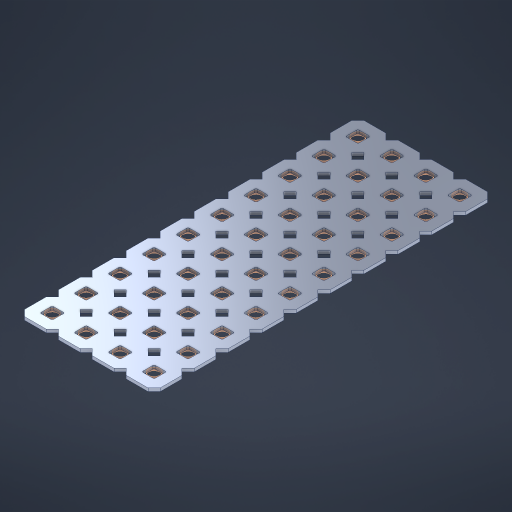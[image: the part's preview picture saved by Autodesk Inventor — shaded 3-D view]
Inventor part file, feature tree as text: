
AUTODESK INVENTOR PART (.ipt)
format: ipt  version: 2023 (Build 270158000, 158)  size: 723,456 bytes
history: native  units: in
note: dims shown in document units (in); Inventor stores cm internally (conversion verified against a paired STEP export)
features: other x41, extrude x39, sketch x2, pattern_linear x1
ambient origin geometry x8: Origin, YZ Plane, XZ Plane, XY Plane, X Axis, Y Axis, Z Axis, Center Point
bodies: Solid1 (feature_tree), Body (feature_tree)
feature tree (83):
  pattern_linear  "Rectangular Pattern1"  Spacing1=0.09in  [1 undecoded]
  sketch  "Sketch1"  dims[d1=0.5in]
  sketch  "Sketch2"  dims[d2=0.182in d3=0.09in d4=0.09in d5=0.09in d6=0.09in d7=0.09in d8=0.09in d9=0.09in d10=0.09in d11=0.02in d13=0.0in d14=0.172in d15=0.0625in d16=0.0in d19=0.5in d22=0.5in]
  other  "Srf1"
  other  "Srf126"
  other  "Srf127"
  other  "Srf128"
  other  "Srf129"
  other  "Srf130"
  other  "Srf131"
  other  "Srf250"
  other  "Srf251"
  other  "Srf252"
  other  "Srf268"
  other  "Srf269"
  other  "Srf270"
  other  "Srf271"
  other  "Srf272"
  other  "Srf273"
  other  "Srf274"
  other  "Srf275"
  other  "Srf276"
  other  "Srf277"
  other  "Srf293"
  other  "Srf294"
  other  "Srf295"
  other  "Srf296"
  other  "Srf297"
  other  "Srf298"
  other  "Srf299"
  other  "Srf300"
  other  "Srf301"
  other  "Srf302"
  other  "Srf318"
  other  "Srf319"
  other  "Srf320"
  other  "Srf321"
  other  "Srf322"
  other  "Srf323"
  other  "Srf324"
  other  "Srf325"
  other  "Srf326"
  other  "Srf327"
  other  "Circle"
  extrude  "ExtrusionSrf126"  Depth=0.09in
  extrude  "ExtrusionSrf127"  Depth=0.09in
  extrude  "ExtrusionSrf128"  Depth=0.09in
  extrude  "ExtrusionSrf129"  Depth=0.09in
  extrude  "ExtrusionSrf130"  Depth=0.09in
  extrude  "ExtrusionSrf131"  Depth=0.09in
  extrude  "ExtrusionSrf250"  Depth=0.09in
  extrude  "ExtrusionSrf251"  Depth=0.02in
  extrude  "ExtrusionSrf252"  TaperAngle=0.0deg  [1 undecoded]
  extrude  "ExtrusionSrf268"  Depth=0.5in
  extrude  "ExtrusionSrf269"  Depth=0.5in TaperAngle=0.0deg
  extrude  "ExtrusionSrf270"  Depth=0.5in
  extrude  "ExtrusionSrf271"  Depth=0.5in
  extrude  "ExtrusionSrf272"  [1 undecoded]
  extrude  "ExtrusionSrf273"  [1 undecoded]
  extrude  "ExtrusionSrf274"  [1 undecoded]
  extrude  "ExtrusionSrf275"  [1 undecoded]
  extrude  "ExtrusionSrf276"  [1 undecoded]
  extrude  "ExtrusionSrf277"  [1 undecoded]
  extrude  "ExtrusionSrf293"  [1 undecoded]
  extrude  "ExtrusionSrf294"  [1 undecoded]
  extrude  "ExtrusionSrf295"  [1 undecoded]
  extrude  "ExtrusionSrf296"  [1 undecoded]
  extrude  "ExtrusionSrf297"  [1 undecoded]
  extrude  "ExtrusionSrf298"  [1 undecoded]
  extrude  "ExtrusionSrf299"  [1 undecoded]
  extrude  "ExtrusionSrf300"  [1 undecoded]
  extrude  "ExtrusionSrf301"  [1 undecoded]
  extrude  "ExtrusionSrf302"  [1 undecoded]
  extrude  "ExtrusionSrf318"  [1 undecoded]
  extrude  "ExtrusionSrf319"  [1 undecoded]
  extrude  "ExtrusionSrf320"  [1 undecoded]
  extrude  "ExtrusionSrf321"  [1 undecoded]
  extrude  "ExtrusionSrf322"  [1 undecoded]
  extrude  "ExtrusionSrf323"  [1 undecoded]
  extrude  "ExtrusionSrf324"  [1 undecoded]
  extrude  "ExtrusionSrf325"  [1 undecoded]
  extrude  "ExtrusionSrf326"  [1 undecoded]
  extrude  "ExtrusionSrf327"  [1 undecoded]
note: 28 required parameter values undecoded (feature->parameter linkage not recoverable at this tier; creation-order binding heuristic only, values carry confidence <= 0.55)
